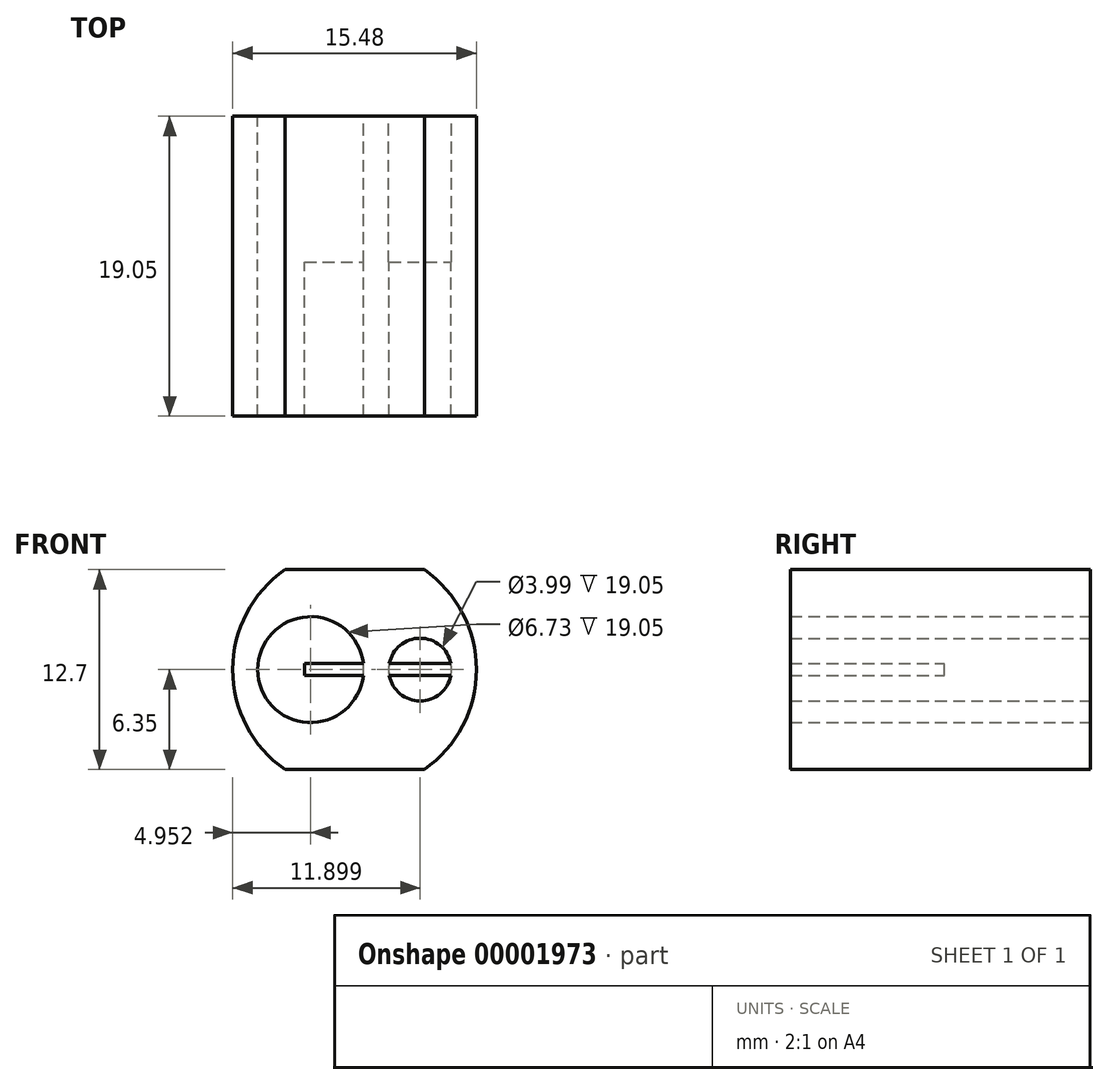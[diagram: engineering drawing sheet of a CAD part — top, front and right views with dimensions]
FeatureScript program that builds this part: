
annotation { "Feature Type Name" : "Feature", "Feature Type Description" : "" }
export const myFeature = defineFeature(function(context is Context, id is Id, definition is map)
    precondition{}
    {
        {
            var Q0;
            Q0=qCreatedBy(makeId("Front.planeOp"),FACE);
            var sketch = newSketch(context, id + "F0", { "sketchPlane" : qUnion([Q0])});
            skCircle(sketch, "E0", {"center": v(-2.79, 0) * mm, "radius": 3.37 * mm});
            skCircle(sketch, "E1", {"center": v(4.16, 0) * mm, "radius": 2 * mm});
            skArc(sketch, "E2", {"start": v(-4.43, 6.35) * mm, "mid": v(-7.74, 0) * mm, "end": v(-4.43, -6.35) * mm});
            skLineSegment(sketch, "E3", {"start": v(-4.43, 6.35) * mm, "end": v(4.43, 6.35) * mm});
            skLineSegment(sketch, "E4", {"start": v(4.43, -6.35) * mm, "end": v(-4.43, -6.35) * mm});
            skLineSegment(sketch, "E5", {"start": v(6.15, 0) * mm, "end": v(-6.15, 0) * mm});
            skArc(sketch, "E6.trimOffspring", {"start": v(4.43, -6.35) * mm, "mid": v(7.74, 0) * mm, "end": v(4.43, 6.35) * mm});
            skLineSegment(sketch, "E7", {"start": v(-6.13, 0.38) * mm, "end": v(0.56, 0.38) * mm});
            skLineSegment(sketch, "E8", {"start": v(6.12, -0.38) * mm, "end": v(2.2, -0.38) * mm});
            skLineSegment(sketch, "E9.trimOffspring", {"start": v(2.2, 0.38) * mm, "end": v(6.12, 0.38) * mm});
            skLineSegment(sketch, "E10.trimOffspring", {"start": v(0.56, -0.38) * mm, "end": v(-6.13, -0.38) * mm});
            skLineSegment(sketch, "E11", {"start": v(-2.4, 0.38) * mm, "end": v(-2.4, -0.38) * mm});
            skLineSegment(sketch, "E12", {"start": v(-3.17, -0.38) * mm, "end": v(-3.17, 0.38) * mm});
            skLineSegment(sketch, "E13", {"start": v(3.78, 0.38) * mm, "end": v(3.78, -0.38) * mm});
            skLineSegment(sketch, "E14", {"start": v(4.54, -0.38) * mm, "end": v(4.54, 0.38) * mm});
            skSolve(sketch);
        }
        {
            var Q0;
            Q0=makeQuery(id+"F0.imprint","IMPRINT",FACE,{"disambiguationData":[TD([[makeQuery(id+"F0.imprint","IMPRINT",EDGE,{"derivedFrom":sQuery(id+"F0.wireOp",EDGE,"E2")}),1.0]])]});
            var Q1;
            {var subQ3=sQuery(id+"F0.wireOp",EDGE,"E7");var subQ5=sQuery(id+"F0.wireOp",EDGE,"E0");var subQ6=makeQuery(id+"F0.imprint","INTERSECT",VERTEX,{"disambiguationData":[OD(1.0)],"derivedFrom":[subQ5,subQ3]});Q1=makeQuery(id+"F0.imprint","IMPRINT",FACE,{"disambiguationData":[TD([[makeQuery(id+"F0.imprint","IMPRINT",EDGE,{"disambiguationData":[TD([[subQ6,1.0]])],"derivedFrom":subQ5}),1.0]])]});}
            var Q2;
            {var subQ3=sQuery(id+"F0.wireOp",EDGE,"E10.trimOffspring");var subQ5=sQuery(id+"F0.wireOp",EDGE,"E0");var subQ6=makeQuery(id+"F0.imprint","INTERSECT",VERTEX,{"disambiguationData":[OD(0.0)],"derivedFrom":[subQ5,subQ3]});Q2=makeQuery(id+"F0.imprint","IMPRINT",FACE,{"disambiguationData":[TD([[makeQuery(id+"F0.imprint","IMPRINT",EDGE,{"disambiguationData":[TD([[subQ6,-1.0]])],"derivedFrom":subQ5}),1.0]])]});}
            var Q3;
            {var subQ1=sQuery(id+"F0.wireOp",EDGE,"E5");var subQ5=sQuery(id+"F0.wireOp",EDGE,"E0");var subQ7=makeQuery(id+"F0.imprint","INTERSECT",VERTEX,{"disambiguationData":[OD(0.0)],"derivedFrom":[subQ5,subQ1]});Q3=makeQuery(id+"F0.imprint","IMPRINT",FACE,{"disambiguationData":[TD([[makeQuery(id+"F0.imprint","IMPRINT",EDGE,{"disambiguationData":[TD([[subQ7,-1.0]])],"derivedFrom":subQ5}),1.0]])]});}
            var Q4;
            {var subQ1=sQuery(id+"F0.wireOp",EDGE,"E5");var subQ5=sQuery(id+"F0.wireOp",EDGE,"E0");var subQ7=makeQuery(id+"F0.imprint","INTERSECT",VERTEX,{"disambiguationData":[OD(0.0)],"derivedFrom":[subQ5,subQ1]});Q4=makeQuery(id+"F0.imprint","IMPRINT",FACE,{"disambiguationData":[TD([[makeQuery(id+"F0.imprint","IMPRINT",EDGE,{"disambiguationData":[TD([[subQ7,1.0]])],"derivedFrom":subQ5}),1.0]])]});}
            var Q5;
            {var subQ1=sQuery(id+"F0.wireOp",EDGE,"E5");var subQ5=sQuery(id+"F0.wireOp",EDGE,"E11");var subQ6=makeQuery(id+"F0.imprint","INTERSECT",VERTEX,{"derivedFrom":[subQ1,subQ5]});Q5=makeQuery(id+"F0.imprint","IMPRINT",FACE,{"disambiguationData":[TD([[makeQuery(id+"F0.imprint","IMPRINT",EDGE,{"disambiguationData":[TD([[subQ6,-1.0]])],"derivedFrom":subQ1}),1.0]])]});}
            var Q6;
            {var subQ1=sQuery(id+"F0.wireOp",EDGE,"E5");var subQ5=sQuery(id+"F0.wireOp",EDGE,"E11");var subQ6=makeQuery(id+"F0.imprint","INTERSECT",VERTEX,{"derivedFrom":[subQ1,subQ5]});Q6=makeQuery(id+"F0.imprint","IMPRINT",FACE,{"disambiguationData":[TD([[makeQuery(id+"F0.imprint","IMPRINT",EDGE,{"disambiguationData":[TD([[subQ6,-1.0]])],"derivedFrom":subQ1}),-1.0]])]});}
            var Q7;
            {var subQ0=sQuery(id+"F0.wireOp",EDGE,"E14");var subQ1=sQuery(id+"F0.wireOp",EDGE,"E5");var subQ2=makeQuery(id+"F0.imprint","INTERSECT",VERTEX,{"derivedFrom":[subQ1,subQ0]});Q7=makeQuery(id+"F0.imprint","IMPRINT",FACE,{"disambiguationData":[TD([[makeQuery(id+"F0.imprint","IMPRINT",EDGE,{"disambiguationData":[TD([[subQ2,-1.0]])],"derivedFrom":subQ1}),1.0]])]});}
            var Q8;
            {var subQ0=sQuery(id+"F0.wireOp",EDGE,"E14");var subQ1=sQuery(id+"F0.wireOp",EDGE,"E5");var subQ2=makeQuery(id+"F0.imprint","INTERSECT",VERTEX,{"derivedFrom":[subQ1,subQ0]});Q8=makeQuery(id+"F0.imprint","IMPRINT",FACE,{"disambiguationData":[TD([[makeQuery(id+"F0.imprint","IMPRINT",EDGE,{"disambiguationData":[TD([[subQ2,-1.0]])],"derivedFrom":subQ1}),-1.0]])]});}
            var Q9;
            {var subQ3=sQuery(id+"F0.wireOp",EDGE,"E9.trimOffspring");var subQ5=sQuery(id+"F0.wireOp",EDGE,"E1");var subQ6=makeQuery(id+"F0.imprint","INTERSECT",VERTEX,{"disambiguationData":[OD(0.0)],"derivedFrom":[subQ5,subQ3]});Q9=makeQuery(id+"F0.imprint","IMPRINT",FACE,{"disambiguationData":[TD([[makeQuery(id+"F0.imprint","IMPRINT",EDGE,{"disambiguationData":[TD([[subQ6,-1.0]])],"derivedFrom":subQ5}),1.0]])]});}
            var Q10;
            {var subQ3=sQuery(id+"F0.wireOp",EDGE,"E8");var subQ5=sQuery(id+"F0.wireOp",EDGE,"E1");var subQ6=makeQuery(id+"F0.imprint","INTERSECT",VERTEX,{"disambiguationData":[OD(1.0)],"derivedFrom":[subQ5,subQ3]});Q10=makeQuery(id+"F0.imprint","IMPRINT",FACE,{"disambiguationData":[TD([[makeQuery(id+"F0.imprint","IMPRINT",EDGE,{"disambiguationData":[TD([[subQ6,1.0]])],"derivedFrom":subQ5}),1.0]])]});}
            var Q11;
            {var subQ1=sQuery(id+"F0.wireOp",EDGE,"E5");var subQ5=sQuery(id+"F0.wireOp",EDGE,"E1");var subQ7=makeQuery(id+"F0.imprint","INTERSECT",VERTEX,{"disambiguationData":[OD(0.0)],"derivedFrom":[subQ5,subQ1]});Q11=makeQuery(id+"F0.imprint","IMPRINT",FACE,{"disambiguationData":[TD([[makeQuery(id+"F0.imprint","IMPRINT",EDGE,{"disambiguationData":[TD([[subQ7,1.0]])],"derivedFrom":subQ5}),1.0]])]});}
            var Q12;
            {var subQ1=sQuery(id+"F0.wireOp",EDGE,"E5");var subQ5=sQuery(id+"F0.wireOp",EDGE,"E1");var subQ7=makeQuery(id+"F0.imprint","INTERSECT",VERTEX,{"disambiguationData":[OD(0.0)],"derivedFrom":[subQ5,subQ1]});Q12=makeQuery(id+"F0.imprint","IMPRINT",FACE,{"disambiguationData":[TD([[makeQuery(id+"F0.imprint","IMPRINT",EDGE,{"disambiguationData":[TD([[subQ7,-1.0]])],"derivedFrom":subQ5}),1.0]])]});}
            extrude(context, id + "F1", {"entities" : qUnion([Q0, Q1, Q2, Q3, Q4, Q5, Q6, Q7, Q8, Q9, Q10, Q11, Q12]), "depth" : 19.05 * mm});
        }
        {
            var Q0;
            {var subQ0=sQuery(id+"F0.wireOp",EDGE,"E10.trimOffspring");var subQ2=sQuery(id+"F0.wireOp",EDGE,"E0");var subQ5=makeQuery(id+"F0.imprint","INTERSECT",VERTEX,{"disambiguationData":[OD(0.0)],"derivedFrom":[subQ2,subQ0]});Q0=makeQuery(id+"F0.imprint","IMPRINT",FACE,{"disambiguationData":[TD([[makeQuery(id+"F0.imprint","IMPRINT",EDGE,{"disambiguationData":[TD([[subQ5,1.0]])],"derivedFrom":subQ2}),1.0]])]});}
            var Q1;
            {var subQ0=sQuery(id+"F0.wireOp",EDGE,"E7");var subQ3=sQuery(id+"F0.wireOp",EDGE,"E0");var subQ5=makeQuery(id+"F0.imprint","INTERSECT",VERTEX,{"disambiguationData":[OD(0.0)],"derivedFrom":[subQ3,subQ0]});Q1=makeQuery(id+"F0.imprint","IMPRINT",FACE,{"disambiguationData":[TD([[makeQuery(id+"F0.imprint","IMPRINT",EDGE,{"disambiguationData":[TD([[subQ5,1.0]])],"derivedFrom":subQ3}),1.0]])]});}
            var Q2;
            {var subQ1=sQuery(id+"F0.wireOp",EDGE,"E5");var subQ5=sQuery(id+"F0.wireOp",EDGE,"E11");var subQ6=makeQuery(id+"F0.imprint","INTERSECT",VERTEX,{"derivedFrom":[subQ1,subQ5]});Q2=makeQuery(id+"F0.imprint","IMPRINT",FACE,{"disambiguationData":[TD([[makeQuery(id+"F0.imprint","IMPRINT",EDGE,{"disambiguationData":[TD([[subQ6,-1.0]])],"derivedFrom":subQ1}),1.0]])]});}
            var Q3;
            {var subQ1=sQuery(id+"F0.wireOp",EDGE,"E5");var subQ5=sQuery(id+"F0.wireOp",EDGE,"E11");var subQ6=makeQuery(id+"F0.imprint","INTERSECT",VERTEX,{"derivedFrom":[subQ1,subQ5]});Q3=makeQuery(id+"F0.imprint","IMPRINT",FACE,{"disambiguationData":[TD([[makeQuery(id+"F0.imprint","IMPRINT",EDGE,{"disambiguationData":[TD([[subQ6,-1.0]])],"derivedFrom":subQ1}),-1.0]])]});}
            var Q4;
            {var subQ1=sQuery(id+"F0.wireOp",EDGE,"E5");var subQ5=sQuery(id+"F0.wireOp",EDGE,"E0");var subQ7=makeQuery(id+"F0.imprint","INTERSECT",VERTEX,{"disambiguationData":[OD(0.0)],"derivedFrom":[subQ5,subQ1]});Q4=makeQuery(id+"F0.imprint","IMPRINT",FACE,{"disambiguationData":[TD([[makeQuery(id+"F0.imprint","IMPRINT",EDGE,{"disambiguationData":[TD([[subQ7,1.0]])],"derivedFrom":subQ5}),1.0]])]});}
            var Q5;
            {var subQ3=sQuery(id+"F0.wireOp",EDGE,"E7");var subQ5=sQuery(id+"F0.wireOp",EDGE,"E0");var subQ6=makeQuery(id+"F0.imprint","INTERSECT",VERTEX,{"disambiguationData":[OD(1.0)],"derivedFrom":[subQ5,subQ3]});Q5=makeQuery(id+"F0.imprint","IMPRINT",FACE,{"disambiguationData":[TD([[makeQuery(id+"F0.imprint","IMPRINT",EDGE,{"disambiguationData":[TD([[subQ6,1.0]])],"derivedFrom":subQ5}),1.0]])]});}
            var Q6;
            {var subQ3=sQuery(id+"F0.wireOp",EDGE,"E10.trimOffspring");var subQ5=sQuery(id+"F0.wireOp",EDGE,"E0");var subQ6=makeQuery(id+"F0.imprint","INTERSECT",VERTEX,{"disambiguationData":[OD(0.0)],"derivedFrom":[subQ5,subQ3]});Q6=makeQuery(id+"F0.imprint","IMPRINT",FACE,{"disambiguationData":[TD([[makeQuery(id+"F0.imprint","IMPRINT",EDGE,{"disambiguationData":[TD([[subQ6,-1.0]])],"derivedFrom":subQ5}),1.0]])]});}
            var Q7;
            {var subQ1=sQuery(id+"F0.wireOp",EDGE,"E5");var subQ5=sQuery(id+"F0.wireOp",EDGE,"E0");var subQ7=makeQuery(id+"F0.imprint","INTERSECT",VERTEX,{"disambiguationData":[OD(0.0)],"derivedFrom":[subQ5,subQ1]});Q7=makeQuery(id+"F0.imprint","IMPRINT",FACE,{"disambiguationData":[TD([[makeQuery(id+"F0.imprint","IMPRINT",EDGE,{"disambiguationData":[TD([[subQ7,-1.0]])],"derivedFrom":subQ5}),1.0]])]});}
            var Q8;
            {var subQ3=sQuery(id+"F0.wireOp",EDGE,"E8");var subQ5=sQuery(id+"F0.wireOp",EDGE,"E1");var subQ6=makeQuery(id+"F0.imprint","INTERSECT",VERTEX,{"disambiguationData":[OD(1.0)],"derivedFrom":[subQ5,subQ3]});Q8=makeQuery(id+"F0.imprint","IMPRINT",FACE,{"disambiguationData":[TD([[makeQuery(id+"F0.imprint","IMPRINT",EDGE,{"disambiguationData":[TD([[subQ6,1.0]])],"derivedFrom":subQ5}),1.0]])]});}
            var Q9;
            {var subQ0=sQuery(id+"F0.wireOp",EDGE,"E14");var subQ1=sQuery(id+"F0.wireOp",EDGE,"E5");var subQ2=makeQuery(id+"F0.imprint","INTERSECT",VERTEX,{"derivedFrom":[subQ1,subQ0]});Q9=makeQuery(id+"F0.imprint","IMPRINT",FACE,{"disambiguationData":[TD([[makeQuery(id+"F0.imprint","IMPRINT",EDGE,{"disambiguationData":[TD([[subQ2,-1.0]])],"derivedFrom":subQ1}),1.0]])]});}
            var Q10;
            {var subQ0=sQuery(id+"F0.wireOp",EDGE,"E14");var subQ1=sQuery(id+"F0.wireOp",EDGE,"E5");var subQ2=makeQuery(id+"F0.imprint","INTERSECT",VERTEX,{"derivedFrom":[subQ1,subQ0]});Q10=makeQuery(id+"F0.imprint","IMPRINT",FACE,{"disambiguationData":[TD([[makeQuery(id+"F0.imprint","IMPRINT",EDGE,{"disambiguationData":[TD([[subQ2,-1.0]])],"derivedFrom":subQ1}),-1.0]])]});}
            var Q11;
            {var subQ1=sQuery(id+"F0.wireOp",EDGE,"E5");var subQ5=sQuery(id+"F0.wireOp",EDGE,"E1");var subQ7=makeQuery(id+"F0.imprint","INTERSECT",VERTEX,{"disambiguationData":[OD(0.0)],"derivedFrom":[subQ5,subQ1]});Q11=makeQuery(id+"F0.imprint","IMPRINT",FACE,{"disambiguationData":[TD([[makeQuery(id+"F0.imprint","IMPRINT",EDGE,{"disambiguationData":[TD([[subQ7,1.0]])],"derivedFrom":subQ5}),1.0]])]});}
            var Q12;
            {var subQ1=sQuery(id+"F0.wireOp",EDGE,"E5");var subQ5=sQuery(id+"F0.wireOp",EDGE,"E1");var subQ7=makeQuery(id+"F0.imprint","INTERSECT",VERTEX,{"disambiguationData":[OD(0.0)],"derivedFrom":[subQ5,subQ1]});Q12=makeQuery(id+"F0.imprint","IMPRINT",FACE,{"disambiguationData":[TD([[makeQuery(id+"F0.imprint","IMPRINT",EDGE,{"disambiguationData":[TD([[subQ7,-1.0]])],"derivedFrom":subQ5}),1.0]])]});}
            var Q13;
            {var subQ3=sQuery(id+"F0.wireOp",EDGE,"E9.trimOffspring");var subQ5=sQuery(id+"F0.wireOp",EDGE,"E1");var subQ6=makeQuery(id+"F0.imprint","INTERSECT",VERTEX,{"disambiguationData":[OD(0.0)],"derivedFrom":[subQ5,subQ3]});Q13=makeQuery(id+"F0.imprint","IMPRINT",FACE,{"disambiguationData":[TD([[makeQuery(id+"F0.imprint","IMPRINT",EDGE,{"disambiguationData":[TD([[subQ6,-1.0]])],"derivedFrom":subQ5}),1.0]])]});}
            extrude(context, id + "F2", {"entities" : qUnion([Q0, Q1, Q2, Q3, Q4, Q5, Q6, Q7, Q8, Q9, Q10, Q11, Q12, Q13]), "operationType" : NewBodyOperationType.REMOVE, "depth" : 9.27 * mm});
        }
        {
            var Q0;
            {var subQ0=sQuery(id+"F0.wireOp",EDGE,"E8");var subQ2=sQuery(id+"F0.wireOp",EDGE,"E1");var subQ5=makeQuery(id+"F0.imprint","INTERSECT",VERTEX,{"disambiguationData":[OD(0.0)],"derivedFrom":[subQ2,subQ0]});Q0=makeQuery(id+"F0.imprint","IMPRINT",FACE,{"disambiguationData":[TD([[makeQuery(id+"F0.imprint","IMPRINT",EDGE,{"disambiguationData":[TD([[subQ5,1.0]])],"derivedFrom":subQ2}),1.0]])]});}
            var Q1;
            {var subQ0=sQuery(id+"F0.wireOp",EDGE,"E9.trimOffspring");var subQ2=sQuery(id+"F0.wireOp",EDGE,"E1");var subQ5=makeQuery(id+"F0.imprint","INTERSECT",VERTEX,{"disambiguationData":[OD(0.0)],"derivedFrom":[subQ2,subQ0]});Q1=makeQuery(id+"F0.imprint","IMPRINT",FACE,{"disambiguationData":[TD([[makeQuery(id+"F0.imprint","IMPRINT",EDGE,{"disambiguationData":[TD([[subQ5,1.0]])],"derivedFrom":subQ2}),1.0]])]});}
            var Q2;
            {var subQ0=sQuery(id+"F0.wireOp",EDGE,"E14");var subQ1=sQuery(id+"F0.wireOp",EDGE,"E5");var subQ2=makeQuery(id+"F0.imprint","INTERSECT",VERTEX,{"derivedFrom":[subQ1,subQ0]});Q2=makeQuery(id+"F0.imprint","IMPRINT",FACE,{"disambiguationData":[TD([[makeQuery(id+"F0.imprint","IMPRINT",EDGE,{"disambiguationData":[TD([[subQ2,-1.0]])],"derivedFrom":subQ1}),1.0]])]});}
            var Q3;
            {var subQ0=sQuery(id+"F0.wireOp",EDGE,"E14");var subQ1=sQuery(id+"F0.wireOp",EDGE,"E5");var subQ2=makeQuery(id+"F0.imprint","INTERSECT",VERTEX,{"derivedFrom":[subQ1,subQ0]});Q3=makeQuery(id+"F0.imprint","IMPRINT",FACE,{"disambiguationData":[TD([[makeQuery(id+"F0.imprint","IMPRINT",EDGE,{"disambiguationData":[TD([[subQ2,-1.0]])],"derivedFrom":subQ1}),-1.0]])]});}
            extrude(context, id + "F3", {"entities" : qUnion([Q0, Q1, Q2, Q3]), "operationType" : NewBodyOperationType.REMOVE, "depth" : 7.87 * mm});
        }
    });
